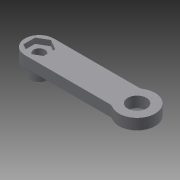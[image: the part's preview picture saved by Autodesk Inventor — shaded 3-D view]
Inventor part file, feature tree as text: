
AUTODESK INVENTOR PART (.ipt)
format: ipt  version: 2014 (Build 180170000, 170)  size: 120,320 bytes
history: native  units: mm
features: extrude x4, sketch x4, other x1, fillet x1
ambient origin geometry x8: Origin, YZ Plane, XZ Plane, XY Plane, X Axis, Y Axis, Z Axis, Center Point
bodies: Body1 (feature_tree)
feature tree (10):
  other  "ソリッド1"
  extrude  "押し出し1"  Depth=27.1mm
  extrude  "押し出し2"  Depth=4.0mm
  extrude  "押し出し3"  Depth=3.2mm
  extrude  "押し出し4"  Depth=5.2mm
  fillet  "フィレット1"  Radius=3.0mm
  sketch  "スケッチ1"
  sketch  "スケッチ3"
  sketch  "スケッチ4"
  sketch  "スケッチ5"
